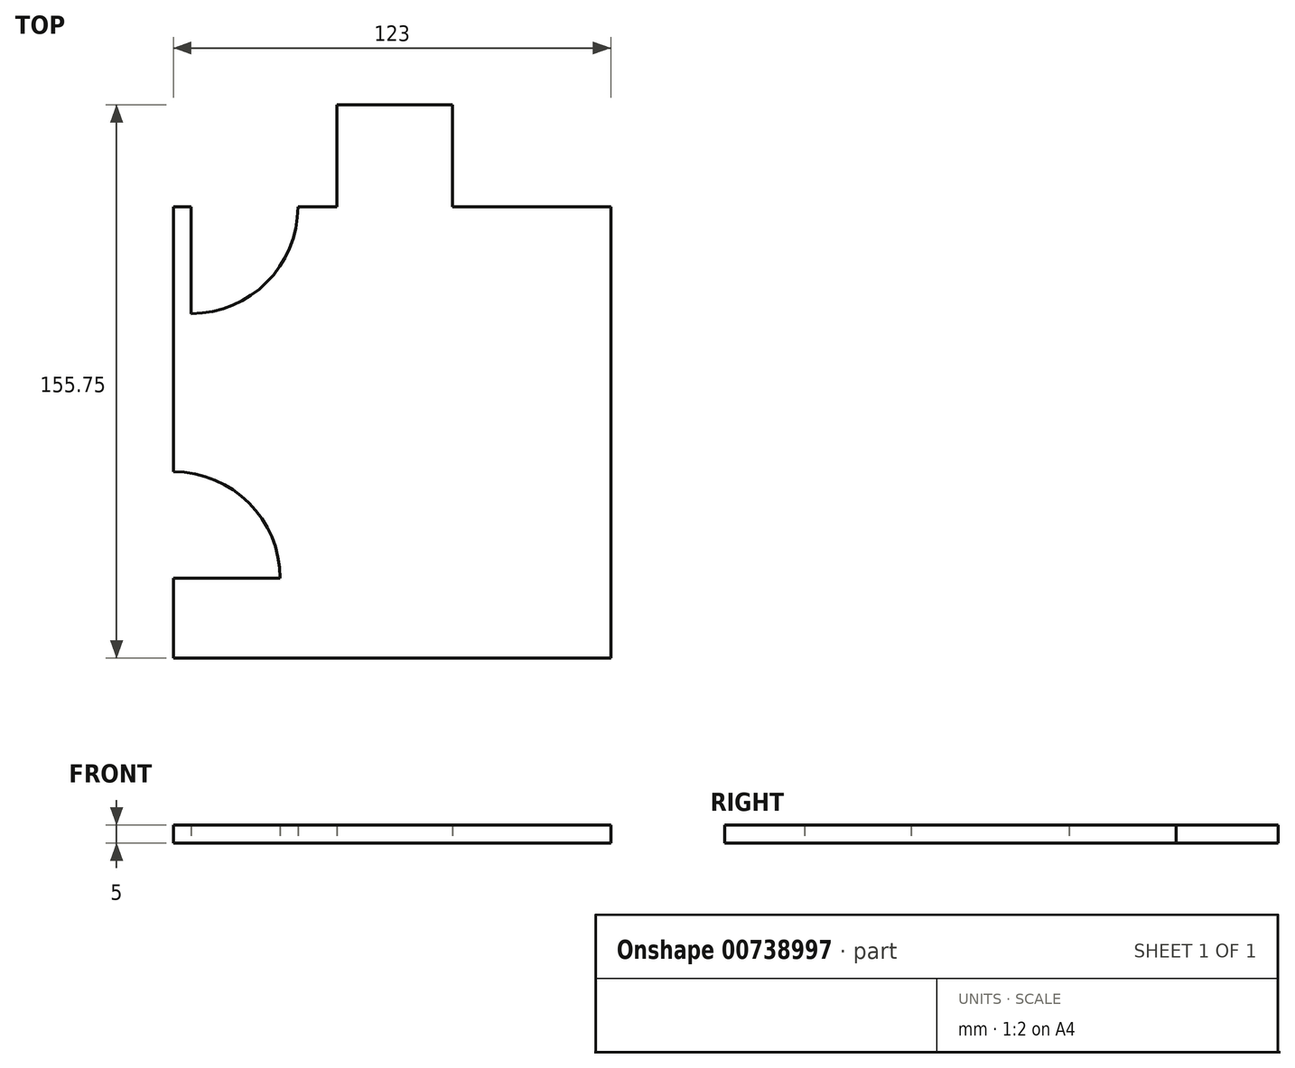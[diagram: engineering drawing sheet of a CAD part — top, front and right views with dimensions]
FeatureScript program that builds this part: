
annotation { "Feature Type Name" : "Feature", "Feature Type Description" : "" }
export const myFeature = defineFeature(function(context is Context, id is Id, definition is map)
    precondition{}
    {
        {
            var Q0;
            Q0=qCreatedBy(makeId("Top.planeOp"),FACE);
            var sketch = newSketch(context, id + "F0", { "sketchPlane" : qUnion([Q0])});
            skLineSegment(sketch, "E0.bottom", {"start": v(61.5, 63.5) * mm, "end": v(17, 63.5) * mm});
            skLineSegment(sketch, "E0.top", {"start": v(61.5, -63.5) * mm, "end": v(-61.5, -63.5) * mm});
            skLineSegment(sketch, "E0.left", {"start": v(61.5, 63.5) * mm, "end": v(61.5, -63.5) * mm});
            skLineSegment(sketch, "E0.right", {"start": v(-61.5, 63.5) * mm, "end": v(-61.5, -11) * mm});
            skPoint(sketch, "E0.middle", {"position": v(0, 0) * mm});
            skLineSegment(sketch, "E1", {"start": v(-56.5, 63.5) * mm, "end": v(-56.5, 33.5) * mm});
            skArc(sketch, "E2", {"start": v(-56.5, 33.5) * mm, "mid": v(-35.29, 42.29) * mm, "end": v(-26.5, 63.5) * mm});
            skLineSegment(sketch, "E3.trimOffspring", {"start": v(-56.5, 63.5) * mm, "end": v(-61.5, 63.5) * mm});
            skLineSegment(sketch, "E4", {"start": v(-15.5, 63.5) * mm, "end": v(-15.5, 92.25) * mm});
            skLineSegment(sketch, "E5", {"start": v(-15.5, 92.25) * mm, "end": v(17, 92.25) * mm});
            skLineSegment(sketch, "E6", {"start": v(17, 92.25) * mm, "end": v(17, 63.5) * mm});
            skLineSegment(sketch, "E7.trimOffspring", {"start": v(-15.5, 63.5) * mm, "end": v(-26.5, 63.5) * mm});
            skLineSegment(sketch, "E8", {"start": v(-61.5, -41) * mm, "end": v(-31.5, -41) * mm});
            skArc(sketch, "E9", {"start": v(-31.5, -41) * mm, "mid": v(-40.29, -19.79) * mm, "end": v(-61.5, -11) * mm});
            skLineSegment(sketch, "E10.trimOffspring", {"start": v(-61.5, -41) * mm, "end": v(-61.5, -63.5) * mm});
            skSolve(sketch);
        }
        {
            var Q0;
            Q0 = qSketchRegion(id + "F0", true);
            extrude(context, id + "F1", {"entities" : qUnion([Q0]), "depth" : 5 * mm, "offsetDistance" : 25 * mm});
        }
    });
